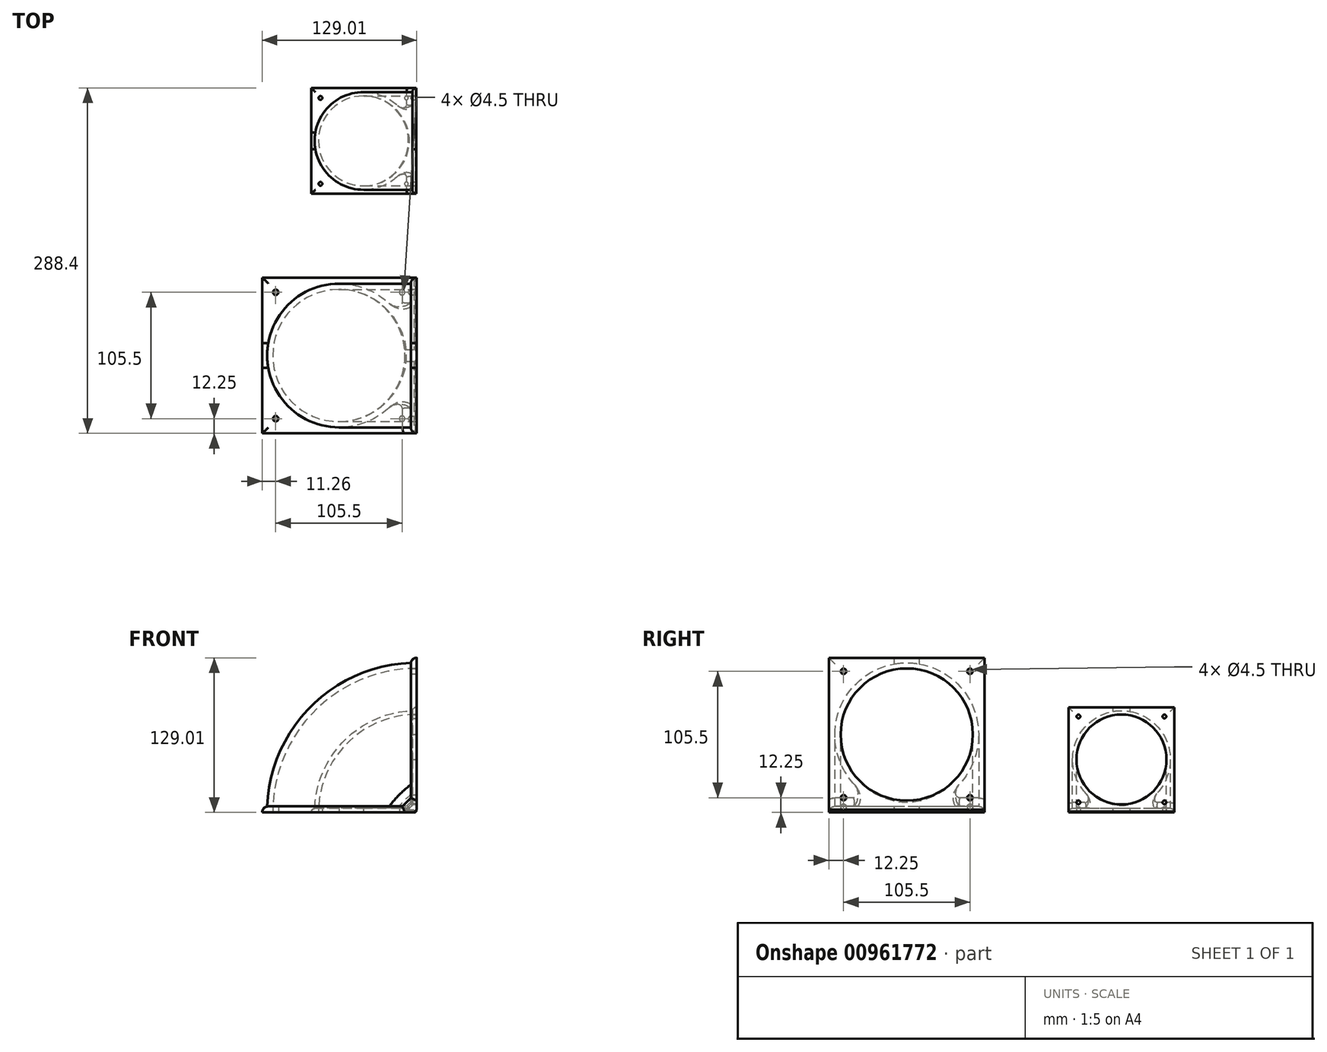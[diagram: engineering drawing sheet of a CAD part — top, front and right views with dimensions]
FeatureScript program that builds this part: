
annotation { "Feature Type Name" : "Feature", "Feature Type Description" : "" }
export const myFeature = defineFeature(function(context is Context, id is Id, definition is map)
    precondition{}
    {
        {
            var Q0;
            Q0=qCreatedBy(makeId("Top.planeOp"),FACE);
            var sketch = newSketch(context, id + "F0", { "sketchPlane" : qUnion([Q0])});
            skCircle(sketch, "E0", {"center": v(0, 0) * mm, "radius": 60 * mm});
            skLineSegment(sketch, "E1.bottom", {"start": v(64.01, -65) * mm, "end": v(-64.01, -65) * mm});
            skLineSegment(sketch, "E1.top", {"start": v(64.01, 65) * mm, "end": v(-64.01, 65) * mm});
            skLineSegment(sketch, "E1.left", {"start": v(64.01, -65) * mm, "end": v(64.01, 65) * mm});
            skLineSegment(sketch, "E1.right", {"start": v(-64.01, -65) * mm, "end": v(-64.01, 65) * mm});
            skCircle(sketch, "E2.0", {"center": v(0, 0) * mm, "radius": 55.2 * mm});
            skLineSegment(sketch, "E3.bottom", {"start": v(52.75, 52.75) * mm, "end": v(-52.75, 52.75) * mm, "construction": true});
            skLineSegment(sketch, "E3.top", {"start": v(52.75, -52.75) * mm, "end": v(-52.75, -52.75) * mm, "construction": true});
            skLineSegment(sketch, "E3.left", {"start": v(52.75, 52.75) * mm, "end": v(52.75, -52.75) * mm, "construction": true});
            skLineSegment(sketch, "E3.right", {"start": v(-52.75, 52.75) * mm, "end": v(-52.75, -52.75) * mm, "construction": true});
            skCircle(sketch, "E4", {"center": v(52.75, -52.75) * mm, "radius": 2.25 * mm});
            skCircle(sketch, "E5", {"center": v(-52.75, -52.75) * mm, "radius": 2.25 * mm});
            skCircle(sketch, "E6", {"center": v(-52.75, 52.75) * mm, "radius": 2.25 * mm});
            skCircle(sketch, "E7", {"center": v(52.75, 52.75) * mm, "radius": 2.25 * mm});
            skSolve(sketch);
        }
        {
            var Q0;
            Q0=qCreatedBy(makeId("Front.planeOp"),FACE);
            var sketch = newSketch(context, id + "F1", { "sketchPlane" : qUnion([Q0])});
            skLineSegment(sketch, "E8.bottom", {"start": v(0, 0) * mm, "end": v(65, 0) * mm, "construction": true});
            skLineSegment(sketch, "E8.top", {"start": v(0, 65) * mm, "end": v(65, 65) * mm, "construction": true});
            skLineSegment(sketch, "E8.left", {"start": v(0, 0) * mm, "end": v(0, 65) * mm, "construction": true});
            skLineSegment(sketch, "E8.right", {"start": v(65, 0) * mm, "end": v(65, 65) * mm, "construction": true});
            skArc(sketch, "E9", {"start": v(19.04, 45.96) * mm, "mid": v(4.95, 24.87) * mm, "end": v(0, 0) * mm});
            skLineSegment(sketch, "E10", {"start": v(0, 65) * mm, "end": v(65, 0) * mm, "construction": true});
            skSolve(sketch);
        }
        {
            var Q0;
            Q0=makeQuery(id+"F0.imprint","IMPRINT",FACE,{"disambiguationData":[TD([[makeQuery(id+"F0.imprint","IMPRINT",EDGE,{"derivedFrom":sQuery(id+"F0.wireOp",EDGE,"E0")}),1.0]])]});
            var Q1;
            Q1=sQuery(id+"F1.wireOp",EDGE,"E9");
            sweep(context, id + "F2", {"profiles" : qUnion([Q0]), "path" : qUnion([Q1])});
        }
        {
            var Q0;
            Q0=makeQuery(id+"F0.imprint","IMPRINT",FACE,{"disambiguationData":[TD([[makeQuery(id+"F0.imprint","IMPRINT",EDGE,{"derivedFrom":sQuery(id+"F0.wireOp",EDGE,"E0")}),1.0]])]});
            var Q1;
            Q1=makeQuery(id+"F0.imprint","IMPRINT",FACE,{"disambiguationData":[TD([[makeQuery(id+"F0.imprint","IMPRINT",EDGE,{"derivedFrom":sQuery(id+"F0.wireOp",EDGE,"E0")}),-1.0]])]});
            extrude(context, id + "F3", {"entities" : qUnion([Q0, Q1]), "operationType" : NewBodyOperationType.ADD, "depth" : 5 * mm, "offsetDistance" : 25 * mm});
        }
        {
            var Q0;
            Q0=makeQuery(id+"F2.opSweep","CAP_FACE",FACE,{"disambiguationData":[OSD([sQuery(id+"F0.wireOp",EDGE,"E0"),sQuery(id+"F0.wireOp",EDGE,"E2.0"),sQuery(id+"F1.wireOp",VERTEX,"E9.start")])],"isStart":false});
            cPlane(context, id + "F4", {"entities" : qUnion([Q0]), "cplaneType" : CPlaneType.OFFSET, "offset" : 0 * mm, "width" : 150 * mm, "height" : 150 * mm});
        }
        {
            var Q0;
            Q0=makeQuery(id+"F2.opSweep","SWEPT_BODY",BODY,{"disambiguationData":[OSD([sQuery(id+"F0.wireOp",EDGE,"E0"),sQuery(id+"F0.wireOp",EDGE,"E2.0"),sQuery(id+"F1.wireOp",EDGE,"E9")])]});
            var Q1;
            Q1=qCreatedBy(id+"F4.planeOp",FACE);
            mirror(context, id + "F5", {"operationType" : NewBodyOperationType.ADD, "entities" : qUnion([Q0]), "mirrorPlane" : qUnion([Q1])});
        }
        {
            var Q0;
            {var subQ0=sQuery(id+"F0.wireOp",EDGE,"E1.top");var subQ1=sQuery(id+"F0.wireOp",EDGE,"E1.bottom");var subQ3=sQuery(id+"F0.wireOp",EDGE,"E6");var subQ4=sQuery(id+"F0.wireOp",EDGE,"E2.0");var subQ5=sQuery(id+"F0.wireOp",EDGE,"E4");var subQ6=sQuery(id+"F0.wireOp",EDGE,"E1.left");var subQ7=sQuery(id+"F0.wireOp",EDGE,"E1.right");var subQ8=sQuery(id+"F0.wireOp",EDGE,"E5");var subQ9=sQuery(id+"F0.wireOp",EDGE,"E7");var subQ10=makeQuery(id+"F3.boolean.opBoolean","SPLIT",FACE,{"disambiguationData":[TD([makeQuery(id+"F3.opExtrude","SWEPT_FACE",FACE,{"disambiguationData":[OSD([subQ1])]})])],"derivedFrom":makeQuery(id+"F3.opExtrude","CAP_FACE",FACE,{"disambiguationData":[OSD([subQ1,subQ0,subQ6,subQ7,subQ4,subQ5,subQ8,subQ3,subQ9])],"isStart":false})});Q0=makeQuery(id+"F5.boolean.opBoolean","INTERSECT",EDGE,{"disambiguationData":[OD(0.0)],"derivedFrom":[subQ10,makeQuery(id+"F5.opPattern","COPY",FACE,{"derivedFrom":subQ10,"instanceName":"1"})]});}
            var Q1;
            {var subQ0=sQuery(id+"F0.wireOp",EDGE,"E1.top");var subQ1=sQuery(id+"F0.wireOp",EDGE,"E1.bottom");var subQ3=sQuery(id+"F0.wireOp",EDGE,"E6");var subQ4=sQuery(id+"F0.wireOp",EDGE,"E2.0");var subQ5=sQuery(id+"F0.wireOp",EDGE,"E4");var subQ6=sQuery(id+"F0.wireOp",EDGE,"E1.left");var subQ7=sQuery(id+"F0.wireOp",EDGE,"E1.right");var subQ8=sQuery(id+"F0.wireOp",EDGE,"E5");var subQ9=sQuery(id+"F0.wireOp",EDGE,"E7");var subQ10=makeQuery(id+"F3.boolean.opBoolean","SPLIT",FACE,{"disambiguationData":[TD([makeQuery(id+"F3.opExtrude","SWEPT_FACE",FACE,{"disambiguationData":[OSD([subQ1])]})])],"derivedFrom":makeQuery(id+"F3.opExtrude","CAP_FACE",FACE,{"disambiguationData":[OSD([subQ1,subQ0,subQ6,subQ7,subQ4,subQ5,subQ8,subQ3,subQ9])],"isStart":false})});Q1=makeQuery(id+"F5.boolean.opBoolean","INTERSECT",EDGE,{"disambiguationData":[OD(1.0)],"derivedFrom":[subQ10,makeQuery(id+"F5.opPattern","COPY",FACE,{"derivedFrom":subQ10,"instanceName":"1"})]});}
            chamfer(context, id + "F6", {"entities" : qUnion([Q0, Q1]), "width" : 7 * mm, "tangentPropagation" : true});
        }
        {
            var Q0;
            {var subQ0=sQuery(id+"F0.wireOp",EDGE,"E0");var subQ1=makeQuery(id+"F2.opSweep","SWEPT_FACE",FACE,{"disambiguationData":[OSD([subQ0,sQuery(id+"F1.wireOp",EDGE,"E9")])]});var subQ2=subQ1;var subQ3=sQuery(id+"F0.wireOp",EDGE,"E1.top");var subQ4=sQuery(id+"F0.wireOp",EDGE,"E1.bottom");var subQ5=sQuery(id+"F0.wireOp",EDGE,"E6");var subQ6=sQuery(id+"F0.wireOp",EDGE,"E2.0");var subQ7=sQuery(id+"F0.wireOp",EDGE,"E4");var subQ8=sQuery(id+"F0.wireOp",EDGE,"E1.left");var subQ9=sQuery(id+"F0.wireOp",EDGE,"E1.right");var subQ10=sQuery(id+"F0.wireOp",EDGE,"E5");var subQ11=sQuery(id+"F0.wireOp",EDGE,"E7");var subQ12=makeQuery(id+"F3.boolean.opBoolean","SPLIT",FACE,{"disambiguationData":[TD([makeQuery(id+"F3.opExtrude","SWEPT_FACE",FACE,{"disambiguationData":[OSD([subQ4])]})])],"derivedFrom":makeQuery(id+"F3.opExtrude","CAP_FACE",FACE,{"disambiguationData":[OSD([subQ4,subQ3,subQ8,subQ9,subQ6,subQ7,subQ10,subQ5,subQ11])],"isStart":false})});Q0=makeQuery(id+"F6.opChamfer","BLEND_EDGE",EDGE,{"blendedFrom":[makeQuery(id+"F5.boolean.opBoolean","INTERSECT",EDGE,{"disambiguationData":[OD(1.0)],"derivedFrom":[subQ12,makeQuery(id+"F5.opPattern","COPY",FACE,{"derivedFrom":subQ12,"instanceName":"1"})]}),makeQuery(id+"F5.boolean.opBoolean","MERGE",FACE,{"derivedFrom":[subQ2,makeQuery(id+"F5.opPattern","COPY",FACE,{"derivedFrom":subQ2,"instanceName":"1"})]})],"blendedInto":[makeQuery(id+"F5.boolean.opBoolean","MERGE",FACE,{"derivedFrom":[subQ2,makeQuery(id+"F5.opPattern","COPY",FACE,{"derivedFrom":subQ2,"instanceName":"1"})]})]});}
            var Q1;
            {var subQ0=sQuery(id+"F0.wireOp",EDGE,"E0");var subQ1=makeQuery(id+"F2.opSweep","SWEPT_FACE",FACE,{"disambiguationData":[OSD([subQ0,sQuery(id+"F1.wireOp",EDGE,"E9")])]});var subQ2=subQ1;var subQ3=sQuery(id+"F0.wireOp",EDGE,"E1.top");var subQ4=sQuery(id+"F0.wireOp",EDGE,"E1.bottom");var subQ5=sQuery(id+"F0.wireOp",EDGE,"E6");var subQ6=sQuery(id+"F0.wireOp",EDGE,"E2.0");var subQ7=sQuery(id+"F0.wireOp",EDGE,"E4");var subQ8=sQuery(id+"F0.wireOp",EDGE,"E1.left");var subQ9=sQuery(id+"F0.wireOp",EDGE,"E1.right");var subQ10=sQuery(id+"F0.wireOp",EDGE,"E5");var subQ11=sQuery(id+"F0.wireOp",EDGE,"E7");var subQ12=makeQuery(id+"F3.boolean.opBoolean","SPLIT",FACE,{"disambiguationData":[TD([makeQuery(id+"F3.opExtrude","SWEPT_FACE",FACE,{"disambiguationData":[OSD([subQ4])]})])],"derivedFrom":makeQuery(id+"F3.opExtrude","CAP_FACE",FACE,{"disambiguationData":[OSD([subQ4,subQ3,subQ8,subQ9,subQ6,subQ7,subQ10,subQ5,subQ11])],"isStart":false})});Q1=makeQuery(id+"F6.opChamfer","BLEND_EDGE",EDGE,{"blendedFrom":[makeQuery(id+"F5.boolean.opBoolean","INTERSECT",EDGE,{"disambiguationData":[OD(0.0)],"derivedFrom":[subQ12,makeQuery(id+"F5.opPattern","COPY",FACE,{"derivedFrom":subQ12,"instanceName":"1"})]}),makeQuery(id+"F5.boolean.opBoolean","MERGE",FACE,{"derivedFrom":[subQ2,makeQuery(id+"F5.opPattern","COPY",FACE,{"derivedFrom":subQ2,"instanceName":"1"})]})],"blendedInto":[makeQuery(id+"F5.boolean.opBoolean","MERGE",FACE,{"derivedFrom":[subQ2,makeQuery(id+"F5.opPattern","COPY",FACE,{"derivedFrom":subQ2,"instanceName":"1"})]})]});}
            var Q2;
            Q2=makeQuery(id+"F3.opExtrude","CAP_EDGE",EDGE,{"disambiguationData":[OSD([sQuery(id+"F0.wireOp",EDGE,"E1.bottom")])],"isStart":false});
            var Q3;
            Q3=makeQuery(id+"F5.opPattern","COPY",EDGE,{"derivedFrom":makeQuery(id+"F3.opExtrude","CAP_EDGE",EDGE,{"disambiguationData":[OSD([sQuery(id+"F0.wireOp",EDGE,"E1.bottom")])],"isStart":false}),"instanceName":"1"});
            var Q4;
            Q4=makeQuery(id+"F5.opPattern","COPY",EDGE,{"derivedFrom":makeQuery(id+"F3.opExtrude","CAP_EDGE",EDGE,{"disambiguationData":[OSD([sQuery(id+"F0.wireOp",EDGE,"E1.top")])],"isStart":false}),"instanceName":"1"});
            var Q5;
            Q5=makeQuery(id+"F5.opPattern","COPY",EDGE,{"derivedFrom":makeQuery(id+"F3.opExtrude","CAP_EDGE",EDGE,{"disambiguationData":[OSD([sQuery(id+"F0.wireOp",EDGE,"E1.right")])],"isStart":false}),"instanceName":"1"});
            var Q6;
            Q6=makeQuery(id+"F3.opExtrude","CAP_EDGE",EDGE,{"disambiguationData":[OSD([sQuery(id+"F0.wireOp",EDGE,"E1.top")])],"isStart":false});
            var Q7;
            {var subQ0=sQuery(id+"F0.wireOp",EDGE,"E1.top");var subQ1=makeQuery(id+"F3.opExtrude","SWEPT_FACE",FACE,{"disambiguationData":[OSD([subQ0])]});var subQ2=sQuery(id+"F0.wireOp",EDGE,"E1.bottom");var subQ4=sQuery(id+"F0.wireOp",EDGE,"E6");var subQ5=sQuery(id+"F0.wireOp",EDGE,"E2.0");var subQ6=sQuery(id+"F0.wireOp",EDGE,"E4");var subQ7=sQuery(id+"F0.wireOp",EDGE,"E1.left");var subQ8=sQuery(id+"F0.wireOp",EDGE,"E1.right");var subQ9=sQuery(id+"F0.wireOp",EDGE,"E5");var subQ10=sQuery(id+"F0.wireOp",EDGE,"E7");var subQ11=makeQuery(id+"F3.boolean.opBoolean","SPLIT",FACE,{"disambiguationData":[TD([makeQuery(id+"F3.opExtrude","SWEPT_FACE",FACE,{"disambiguationData":[OSD([subQ2])]})])],"derivedFrom":makeQuery(id+"F3.opExtrude","CAP_FACE",FACE,{"disambiguationData":[OSD([subQ2,subQ0,subQ7,subQ8,subQ5,subQ6,subQ9,subQ4,subQ10])],"isStart":false})});Q7=makeQuery(id+"F6.opChamfer","BLEND_EDGE",EDGE,{"blendedFrom":[makeQuery(id+"F5.boolean.opBoolean","INTERSECT",EDGE,{"disambiguationData":[OD(1.0)],"derivedFrom":[subQ11,makeQuery(id+"F5.opPattern","COPY",FACE,{"derivedFrom":subQ11,"instanceName":"1"})]}),makeQuery(id+"F5.boolean.opBoolean","MERGE",FACE,{"derivedFrom":[subQ1,makeQuery(id+"F5.opPattern","COPY",FACE,{"derivedFrom":subQ1,"instanceName":"1"})]})],"blendedInto":[makeQuery(id+"F5.boolean.opBoolean","MERGE",FACE,{"derivedFrom":[subQ1,makeQuery(id+"F5.opPattern","COPY",FACE,{"derivedFrom":subQ1,"instanceName":"1"})]})]});}
            var Q8;
            {var subQ0=sQuery(id+"F0.wireOp",EDGE,"E1.bottom");var subQ1=makeQuery(id+"F3.opExtrude","SWEPT_FACE",FACE,{"disambiguationData":[OSD([subQ0])]});var subQ2=sQuery(id+"F0.wireOp",EDGE,"E1.top");var subQ4=sQuery(id+"F0.wireOp",EDGE,"E6");var subQ5=sQuery(id+"F0.wireOp",EDGE,"E2.0");var subQ6=sQuery(id+"F0.wireOp",EDGE,"E4");var subQ7=sQuery(id+"F0.wireOp",EDGE,"E1.left");var subQ8=sQuery(id+"F0.wireOp",EDGE,"E1.right");var subQ9=sQuery(id+"F0.wireOp",EDGE,"E5");var subQ10=sQuery(id+"F0.wireOp",EDGE,"E7");var subQ11=makeQuery(id+"F3.boolean.opBoolean","SPLIT",FACE,{"disambiguationData":[TD([subQ1])],"derivedFrom":makeQuery(id+"F3.opExtrude","CAP_FACE",FACE,{"disambiguationData":[OSD([subQ0,subQ2,subQ7,subQ8,subQ5,subQ6,subQ9,subQ4,subQ10])],"isStart":false})});Q8=makeQuery(id+"F6.opChamfer","BLEND_EDGE",EDGE,{"blendedFrom":[makeQuery(id+"F5.boolean.opBoolean","INTERSECT",EDGE,{"disambiguationData":[OD(0.0)],"derivedFrom":[subQ11,makeQuery(id+"F5.opPattern","COPY",FACE,{"derivedFrom":subQ11,"instanceName":"1"})]}),makeQuery(id+"F5.boolean.opBoolean","MERGE",FACE,{"derivedFrom":[subQ1,makeQuery(id+"F5.opPattern","COPY",FACE,{"derivedFrom":subQ1,"instanceName":"1"})]})],"blendedInto":[makeQuery(id+"F5.boolean.opBoolean","MERGE",FACE,{"derivedFrom":[subQ1,makeQuery(id+"F5.opPattern","COPY",FACE,{"derivedFrom":subQ1,"instanceName":"1"})]})]});}
            var Q9;
            Q9=makeQuery(id+"F3.opExtrude","CAP_EDGE",EDGE,{"disambiguationData":[OSD([sQuery(id+"F0.wireOp",EDGE,"E1.right")])],"isStart":false});
            fillet(context, id + "F7", {"entities" : qUnion([Q0, Q1, Q2, Q3, Q4, Q5, Q6, Q7, Q8, Q9]), "radius" : 5 * mm, "tangentPropagation" : true, "allowEdgeOverflow" : false});
        }
        {
            var Q0;
            Q0=makeQuery(id+"F2.opSweep","SWEPT_BODY",BODY,{"disambiguationData":[OSD([sQuery(id+"F0.wireOp",EDGE,"E0"),sQuery(id+"F0.wireOp",EDGE,"E2.0"),sQuery(id+"F1.wireOp",EDGE,"E9")])]});
            transform(context, id + "F8", {"entities" : qUnion([Q0]), "transformType" : TransformType.TRANSLATION_3D, "dx" : 0 * mm, "dy" : 200 * mm, "dz" : 0 * mm, "makeCopy" : true});
        }
        {
            var Q0;
            Q0=makeQuery(id+"F8.opPattern","COPY",BODY,{"derivedFrom":makeQuery(id+"F2.opSweep","SWEPT_BODY",BODY,{"disambiguationData":[OSD([sQuery(id+"F0.wireOp",EDGE,"E0"),sQuery(id+"F0.wireOp",EDGE,"E2.0"),sQuery(id+"F1.wireOp",EDGE,"E9")])]}),"instanceName":"1"});
            var Q1;
            Q1=makeQuery(id+"F8.opPattern","COPY",VERTEX,{"derivedFrom":makeQuery(id+"F3.opExtrude","CAP_VERTEX",VERTEX,{"disambiguationData":[OSD([sQuery(id+"F0.wireOp",EDGE,"E1.bottom"),sQuery(id+"F0.wireOp",EDGE,"E1.left")])],"isStart":true}),"instanceName":"1"});
            transform(context, id + "F9", {"entities" : qUnion([Q0]), "transformType" : TransformType.SCALE_UNIFORMLY, "scale" : 0.68, "scalePoint" : qUnion([Q1]), "makeCopy" : false});
        }
        {
            var Q0;
            {var subQ0=sQuery(id+"F0.wireOp",EDGE,"E2.0");Q0=makeQuery(id+"F5.opPattern","COPY",FACE,{"derivedFrom":makeQuery(id+"F3.boolean.opBoolean","MERGE",FACE,{"derivedFrom":[makeQuery(id+"F2.opSweep","CAP_FACE",FACE,{"disambiguationData":[OSD([sQuery(id+"F0.wireOp",EDGE,"E0"),subQ0,sQuery(id+"F1.wireOp",VERTEX,"E9.end")])],"isStart":true}),makeQuery(id+"F3.opExtrude","CAP_FACE",FACE,{"disambiguationData":[OSD([sQuery(id+"F0.wireOp",EDGE,"E1.bottom"),sQuery(id+"F0.wireOp",EDGE,"E1.top"),sQuery(id+"F0.wireOp",EDGE,"E1.left"),sQuery(id+"F0.wireOp",EDGE,"E1.right"),subQ0,sQuery(id+"F0.wireOp",EDGE,"E4"),sQuery(id+"F0.wireOp",EDGE,"E5"),sQuery(id+"F0.wireOp",EDGE,"E6"),sQuery(id+"F0.wireOp",EDGE,"E7")])],"isStart":true})]}),"instanceName":"1"});}
            var sketch = newSketch(context, id + "F10", { "sketchPlane" : qUnion([Q0])});
            skArc(sketch, "E11", {"start": v(5, 0.99) * mm, "mid": v(0, 2.33) * mm, "end": v(-5, 0.99) * mm});
            skLineSegment(sketch, "E12", {"start": v(-5, 0.99) * mm, "end": v(-5, 0) * mm});
            skLineSegment(sketch, "E13", {"start": v(-5, 0) * mm, "end": v(5, 0) * mm});
            skLineSegment(sketch, "E14", {"start": v(5, 0) * mm, "end": v(5, 0.99) * mm});
            skSolve(sketch);
        }
        {
            var Q0;
            {var subQ0=sQuery(id+"F10.wireOp",EDGE,"E11");Q0=makeQuery(id+"F10.imprint","IMPRINT",FACE,{"disambiguationData":[TD([[makeQuery(id+"F10.imprint","IMPRINT",EDGE,{"derivedFrom":subQ0}),1.0]])]});}
            var Q1;
            {var subQ0=sQuery(id+"F10.wireOp",EDGE,"E12");Q1=makeQuery(id+"F10.imprint","IMPRINT",FACE,{"disambiguationData":[TD([[makeQuery(id+"F10.imprint","IMPRINT",EDGE,{"derivedFrom":subQ0}),1.0]])]});}
            extrude(context, id + "F11", {"entities" : qUnion([Q0, Q1]), "operationType" : NewBodyOperationType.REMOVE, "oppositeDirection" : true, "depth" : 25 * mm, "offsetDistance" : 25 * mm});
        }
        {
            var Q0;
            {var subQ1=sQuery(id+"F0.wireOp",EDGE,"E1.left");var subQ2=sQuery(id+"F0.wireOp",EDGE,"E1.top");var subQ3=makeQuery(id+"F3.opExtrude","SWEPT_FACE",FACE,{"disambiguationData":[OSD([subQ2])]});Q0=makeQuery(id+"F11.boolean.opBoolean","SPLIT",EDGE,{"disambiguationData":[TD([subQ3])],"derivedFrom":makeQuery(id+"F5.opPattern","COPY",EDGE,{"derivedFrom":makeQuery(id+"F3.opExtrude","CAP_EDGE",EDGE,{"disambiguationData":[OSD([subQ1])],"isStart":true}),"instanceName":"1"})});}
            var Q1;
            {var subQ1=sQuery(id+"F0.wireOp",EDGE,"E1.left");var subQ2=sQuery(id+"F0.wireOp",EDGE,"E1.bottom");var subQ3=makeQuery(id+"F3.opExtrude","SWEPT_FACE",FACE,{"disambiguationData":[OSD([subQ2])]});Q1=makeQuery(id+"F11.boolean.opBoolean","SPLIT",EDGE,{"disambiguationData":[TD([subQ3])],"derivedFrom":makeQuery(id+"F5.opPattern","COPY",EDGE,{"derivedFrom":makeQuery(id+"F3.opExtrude","CAP_EDGE",EDGE,{"disambiguationData":[OSD([subQ1])],"isStart":true}),"instanceName":"1"})});}
            chamfer(context, id + "F12", {"entities" : qUnion([Q0, Q1]), "width" : 1.33 * mm, "tangentPropagation" : true});
        }
        {
            var Q0;
            {var subQ0=sQuery(id+"F0.wireOp",EDGE,"E1.left");var subQ2=sQuery(id+"F0.wireOp",EDGE,"E1.bottom");var subQ3=makeQuery(id+"F3.opExtrude","SWEPT_FACE",FACE,{"disambiguationData":[OSD([subQ2])]});Q0=makeQuery(id+"F11.boolean.opBoolean","SPLIT",EDGE,{"disambiguationData":[TD([subQ3])],"derivedFrom":makeQuery(id+"F3.opExtrude","CAP_EDGE",EDGE,{"disambiguationData":[OSD([subQ0])],"isStart":true})});}
            var Q1;
            {var subQ0=sQuery(id+"F0.wireOp",EDGE,"E1.left");var subQ1=sQuery(id+"F0.wireOp",EDGE,"E1.top");var subQ2=makeQuery(id+"F3.opExtrude","SWEPT_FACE",FACE,{"disambiguationData":[OSD([subQ1])]});Q1=makeQuery(id+"F11.boolean.opBoolean","SPLIT",EDGE,{"disambiguationData":[TD([subQ2])],"derivedFrom":makeQuery(id+"F3.opExtrude","CAP_EDGE",EDGE,{"disambiguationData":[OSD([subQ0])],"isStart":true})});}
            chamfer(context, id + "F13", {"entities" : qUnion([Q0, Q1]), "width" : 1.31 * mm, "tangentPropagation" : true});
        }
    });
